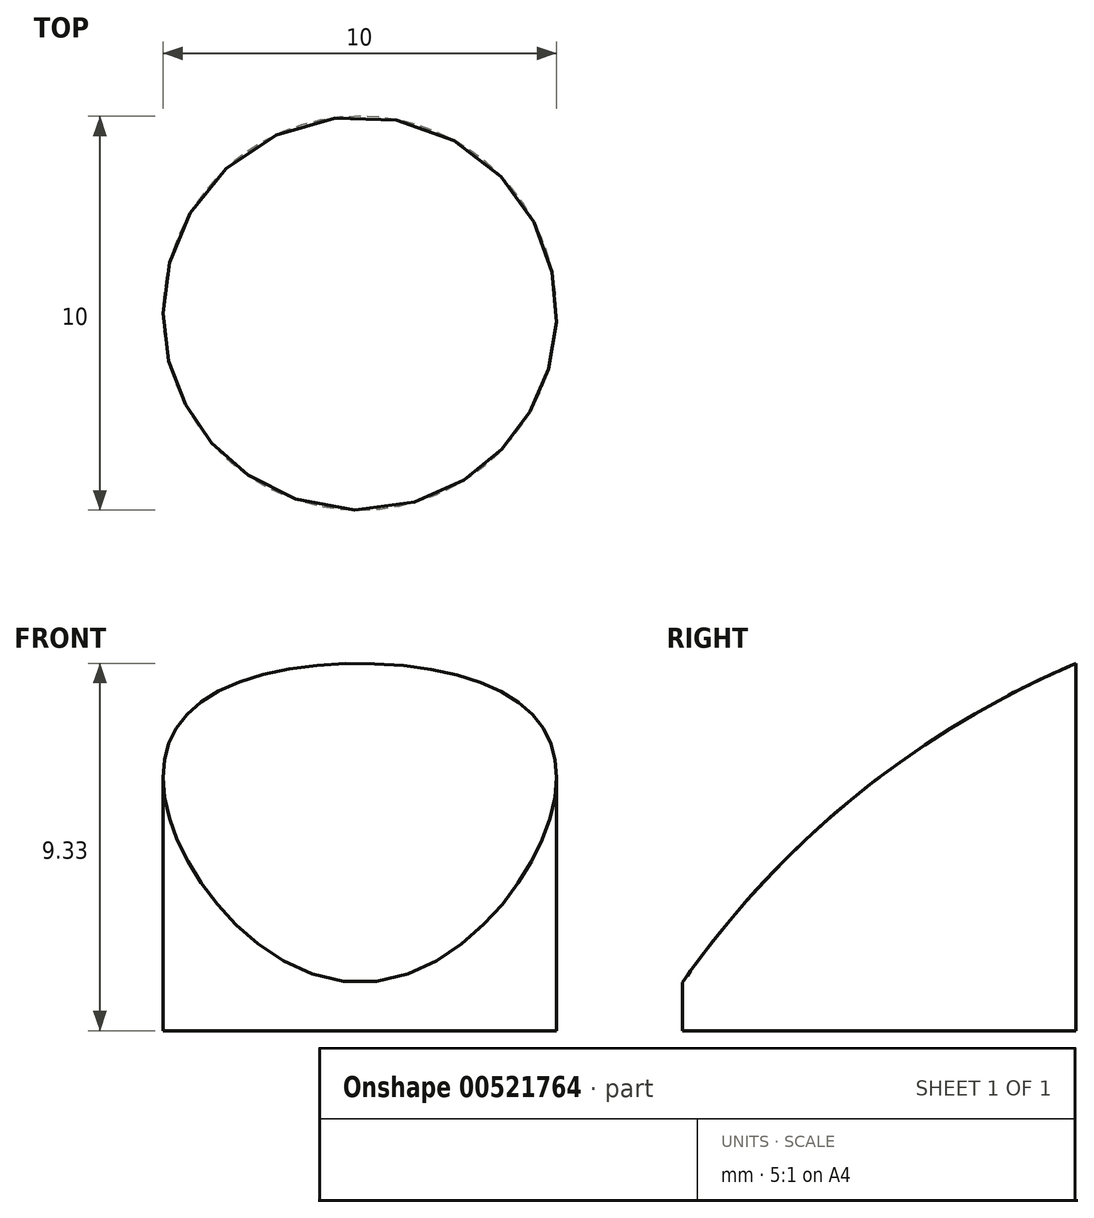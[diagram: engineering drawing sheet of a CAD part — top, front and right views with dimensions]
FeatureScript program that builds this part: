
annotation { "Feature Type Name" : "Feature", "Feature Type Description" : "" }
export const myFeature = defineFeature(function(context is Context, id is Id, definition is map)
    precondition{}
    {
        {
            var Q0;
            Q0=qCreatedBy(makeId("Top.planeOp"),FACE);
            var sketch = newSketch(context, id + "F0", { "sketchPlane" : qUnion([Q0])});
            skCircle(sketch, "E0", {"center": v(0, 0) * mm, "radius": 5 * mm});
            skSolve(sketch);
        }
        {
            var Q0;
            Q0 = qSketchRegion(id + "F0", true);
            extrude(context, id + "F1", {"entities" : qUnion([Q0]), "depth" : 25 * mm, "offsetDistance" : 25 * mm});
        }
        {
            var Q0;
            Q0=qCreatedBy(makeId("Right.planeOp"),FACE);
            var sketch = newSketch(context, id + "F2", { "sketchPlane" : qUnion([Q0])});
            skCircle(sketch, "E1", {"center": v(14, -12) * mm, "radius": 23.15 * mm});
            skCircle(sketch, "E2", {"center": v(14, -12) * mm, "radius": 100 * mm});
            skSolve(sketch);
        }
        {
            var Q0;
            Q0=makeQuery(id+"F2.imprint","IMPRINT",FACE,{"disambiguationData":[TD([[makeQuery(id+"F2.imprint","IMPRINT",EDGE,{"derivedFrom":sQuery(id+"F2.wireOp",EDGE,"E1")}),-1.0]])]});
            extrude(context, id + "F3", {"entities" : qUnion([Q0]), "operationType" : NewBodyOperationType.REMOVE, "oppositeDirection" : true, "depth" : 25 * mm, "offsetDistance" : 25 * mm, "hasSecondDirection" : true, "secondDirectionOppositeDirection" : false, "secondDirectionDepth" : 25 * mm});
        }
    });
